# Revit family: Plumbing Fixture-Grease_Interseptor_Mifab_MI-RICE
name_source: partatom
category: Plumbing Fixtures
revit_build: Autodesk Revit Structure 2013 (Build: 20120221_2030(x64)
units: mm (PartAtom-declared; Revit-internal decimal feet)

## types (12) — shared parameters
Assembly Code = D2090300
Description = Rice Interceptor
Interceptor Material = Acid Resistant Epoxy Coated Green
Manufacturer = MIFAB
URL = www.mifab.com
zero-valued in all types: Default Elevation, WFU

## per-type parameters (varying)
| type | A | B | C | D | E | F | Flow Rate | Standard Inlet And Outlet Radii |
| MI-RICE-1 | 29.5 " | 20 " | 3 " | 17 " | 20 " | 2 " | 34 GPM | 1 " |
| MI-RICE-2 | 29.5 " | 20.5 " | 4 " | 20 " | 24 " | 3 " | 40 GPM | 1.5 " |
| MI-RICE-3 | 33.5 " | 26 " | 4 " | 26 " | 30 " | 3 " | 80 GPM | 1.5 " |
| MI-RICE-4 | 37.5 " | 30 " | 4 " | 28 " | 32 " | 3 " | 111 GPM | 1.5 " |
| MI-RICE-5 | 55.5 " | 26 " | 6 " | 30 " | 36 " | 4 " | 155 GPM | 2 " |
| MI-RICE-6 | 67.5 " | 28 " | 8 " | 32 " | 40 " | 6 " | 213 GPM | 3 " |
| MI-RICE-7 | 67.5 " | 28 " | 10 " | 44 " | 54 " | 6 " | 302 GPM | 3 " |
| MI-RICE-8 | 67.5 " | 30 " | 12 " | 54 " | 66 " | 6 " | 405 GPM | 3 " |
| MI-RICE-9 | 67.5 " | 40 " | 10 " | 50 " | 60 " | 6 " | 506 GPM | 3 " |
| MI-RICE-10 | 91.5 " | 40 " | 8 " | 54 " | 62 " | 6 " | 750 GPM | 3 " |
| MI-RICE-11 | 98 " | 50 " | 12 " | 54 " | 66 " | 6 " | 1017 GPM | 3 " |
| MI-RICE-12 | 98 " | 50 " | 12 " | 80 " | 92 " | 6 " | 1536 GPM | 3 " |

note: column(s) folded — value = type name in every type: Model

## geometry (parser evidence)
native form markers: Blend x7, Sweep x1
no freeform markers — native parametric forms only
